# Revit family: xxFaucet-American_Standard-Studio_S-7105.101
name_source: partatom
category: Plumbing Fixtures
revit_build: Autodesk Revit 2014 (Build: 20130308_1515(x64)
units: mm (PartAtom-declared; Revit-internal decimal feet)

## types (1)
- 7105.101
    ADA Compliant = Yes
    Assembly Code = D2020300
    CW Connection = Yes
    CWFU = 1.5
    Cold Water Connection Diameter = 3/8"
    Default Elevation = 0"
    Description = Studio S Single Control Lavatory Faucet. Lever Handle. Metal Speed Connect pop-up drain.
    Finish = Brass-American Standard-002-Polished Chrome
    Flow Rate = 1.2 gpm/ 4.5 L/min.
    HW Connection = Yes
    HWFU = 1.5
    Height = 7"
    Hot Water Connection Diameter = 0"
    Installation Type = Deck Mounted
    Length = 7 5/16"
    Manufacturer = American Standard
    Material = Brass-American Standard-002-Polished Chrome
    Model = 7105.101
    Price = Prices may vary. Please consult Manufacturer Representative for most up-to-date price list.
    Product Documentation Link = https://www.americanstandard-us.com
    Product Page URL = https://www.americanstandard-us.com
    Specification = Single control lavatory faucet shall feature a brass body and metal lever handle. Fitting shall be equipped with flexible supplies with 3/8in compression connectors. Shall also feature washerless ceramic disc valve cartridge with an integral hot limit safety stop. Shall also feature a metal drain body with stainless steel cable actuation.
    URL = https://www.americanstandard-us.com
    Vent Connection = No
    WFU = 2
    Warranty Information = Limited Lifetime Function and Finish Warranty
    Waste Connection = No
    Width = 1 1/4"

## geometry (parser evidence)
native form markers: Sweep x1
no freeform markers — native parametric forms only
